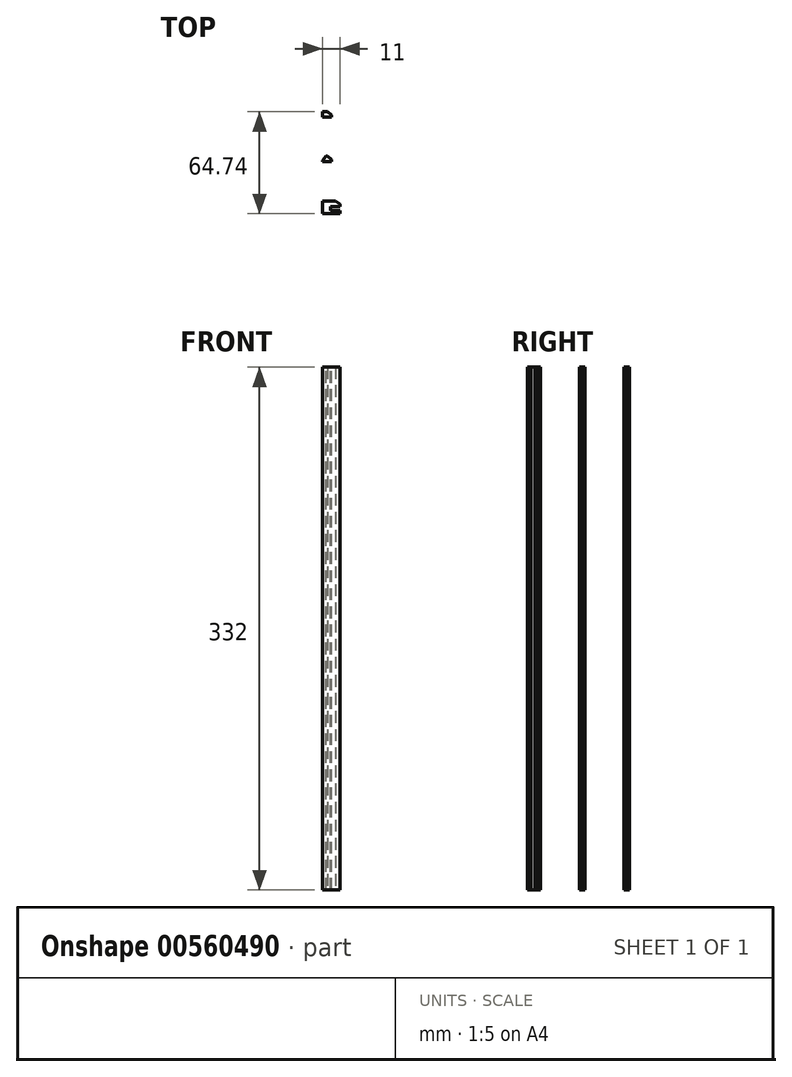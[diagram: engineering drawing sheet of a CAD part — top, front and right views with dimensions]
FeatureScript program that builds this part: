
annotation { "Feature Type Name" : "Feature", "Feature Type Description" : "" }
export const myFeature = defineFeature(function(context is Context, id is Id, definition is map)
    precondition{}
    {
        {
            var Q0;
            Q0=qCreatedBy(makeId("Top.planeOp"),FACE);
            var sketch = newSketch(context, id + "F0", { "sketchPlane" : qUnion([Q0])});
            skLineSegment(sketch, "E0.bottom", {"start": v(45.75, 4) * mm, "end": v(-45.75, 4) * mm});
            skLineSegment(sketch, "E0.top", {"start": v(45.75, -4) * mm, "end": v(-45.75, -4) * mm});
            skLineSegment(sketch, "E0.left", {"start": v(45.75, 4) * mm, "end": v(45.75, -4) * mm});
            skLineSegment(sketch, "E0.right", {"start": v(-45.75, 4) * mm, "end": v(-45.75, -4) * mm});
            skPoint(sketch, "E0.middle", {"position": v(0, 0) * mm});
            skLineSegment(sketch, "E1.bottom", {"start": v(45.75, -2) * mm, "end": v(39.75, -2) * mm});
            skLineSegment(sketch, "E1.top", {"start": v(45.75, 0.6) * mm, "end": v(39.75, 0.6) * mm});
            skLineSegment(sketch, "E1.left", {"start": v(45.75, -2) * mm, "end": v(45.75, 0.6) * mm});
            skLineSegment(sketch, "E1.right", {"start": v(39.75, -2) * mm, "end": v(39.75, 0.6) * mm});
            skPoint(sketch, "E1.middle", {"position": v(42.75, -0.7) * mm});
            skLineSegment(sketch, "E2.bottom", {"start": v(-45.75, -4) * mm, "end": v(-40.25, -4) * mm});
            skLineSegment(sketch, "E2.top", {"start": v(-45.75, -2) * mm, "end": v(-40.25, -2) * mm});
            skLineSegment(sketch, "E2.left", {"start": v(-45.75, -4) * mm, "end": v(-45.75, -2) * mm});
            skLineSegment(sketch, "E2.right", {"start": v(-40.25, -4) * mm, "end": v(-40.25, -2) * mm});
            skLineSegment(sketch, "E3.bottom", {"start": v(-45.75, 0.5) * mm, "end": v(-40.25, 0.5) * mm});
            skLineSegment(sketch, "E3.top", {"start": v(-45.75, 4) * mm, "end": v(-40.25, 4) * mm});
            skLineSegment(sketch, "E3.left", {"start": v(-45.75, 0.5) * mm, "end": v(-45.75, 4) * mm});
            skLineSegment(sketch, "E3.right", {"start": v(-40.25, 0.5) * mm, "end": v(-40.25, 4) * mm});
            skLineSegment(sketch, "E4.bottom", {"start": v(-34.82, -24.44) * mm, "end": v(-45.82, -24.44) * mm});
            skLineSegment(sketch, "E4.top", {"start": v(-34.82, -32.44) * mm, "end": v(-45.82, -32.44) * mm});
            skLineSegment(sketch, "E4.left", {"start": v(-34.82, -24.44) * mm, "end": v(-34.82, -32.44) * mm});
            skLineSegment(sketch, "E4.right", {"start": v(-45.82, -24.44) * mm, "end": v(-45.82, -32.44) * mm});
            skPoint(sketch, "E4.middle", {"position": v(-40.32, -28.44) * mm});
            skLineSegment(sketch, "E5.bottom", {"start": v(-34.82, -30.44) * mm, "end": v(-40.82, -30.44) * mm});
            skLineSegment(sketch, "E5.top", {"start": v(-34.82, -27.84) * mm, "end": v(-40.82, -27.84) * mm});
            skLineSegment(sketch, "E5.left", {"start": v(-34.82, -30.44) * mm, "end": v(-34.82, -27.84) * mm});
            skLineSegment(sketch, "E5.right", {"start": v(-40.82, -30.44) * mm, "end": v(-40.82, -27.84) * mm});
            skPoint(sketch, "E5.middle", {"position": v(-37.82, -29.14) * mm});
            skLineSegment(sketch, "E6.bottom", {"start": v(-45.82, -32.44) * mm, "end": v(-40.32, -32.44) * mm});
            skLineSegment(sketch, "E6.left", {"start": v(-45.82, -32.44) * mm, "end": v(-45.82, -30.44) * mm});
            skLineSegment(sketch, "E7.top", {"start": v(-45.82, -24.44) * mm, "end": v(-40.32, -24.44) * mm});
            skPoint(sketch, "E8.middle", {"position": v(-0.95, -28.36) * mm});
            skLineSegment(sketch, "E9.bottom", {"start": v(-29.23, 32.3) * mm, "end": v(-45.73, 32.3) * mm});
            skLineSegment(sketch, "E9.top", {"start": v(-29.23, 24.3) * mm, "end": v(-45.73, 24.3) * mm});
            skLineSegment(sketch, "E9.left", {"start": v(-29.23, 32.3) * mm, "end": v(-29.23, 24.3) * mm});
            skLineSegment(sketch, "E9.right", {"start": v(-45.73, 32.3) * mm, "end": v(-45.73, 24.3) * mm});
            skPoint(sketch, "E9.middle", {"position": v(-37.48, 28.3) * mm});
            skLineSegment(sketch, "E10.left", {"start": v(-29.23, 26.3) * mm, "end": v(-29.23, 28.9) * mm});
            skLineSegment(sketch, "E11.bottom", {"start": v(-45.73, 24.3) * mm, "end": v(-40.23, 24.3) * mm});
            skLineSegment(sketch, "E11.top", {"start": v(-45.73, 26.3) * mm, "end": v(-40.23, 26.3) * mm});
            skLineSegment(sketch, "E11.left", {"start": v(-45.73, 24.3) * mm, "end": v(-45.73, 26.3) * mm});
            skLineSegment(sketch, "E11.right", {"start": v(-40.23, 24.3) * mm, "end": v(-40.23, 26.3) * mm});
            skLineSegment(sketch, "E12.bottom", {"start": v(-45.73, 28.8) * mm, "end": v(-40.23, 28.8) * mm});
            skLineSegment(sketch, "E12.top", {"start": v(-45.73, 32.3) * mm, "end": v(-40.23, 32.3) * mm});
            skLineSegment(sketch, "E12.left", {"start": v(-45.73, 28.8) * mm, "end": v(-45.73, 32.3) * mm});
            skLineSegment(sketch, "E12.right", {"start": v(-40.23, 28.8) * mm, "end": v(-40.23, 32.3) * mm});
            skSolve(sketch);
        }
        {
            var Q0;
            {var subQ2=sQuery(id+"F0.wireOp",EDGE,"E0.bottom");Q0=makeQuery(id+"F0.imprint","IMPRINT",FACE,{"disambiguationData":[TD([[makeQuery(id+"F0.imprint","IMPRINT",EDGE,{"derivedFrom":subQ2}),1.0]])]});}
            extrude(context, id + "F1", {"entities" : qUnion([Q0]), "oppositeDirection" : true, "depth" : 332 * mm, "offsetDistance" : 25 * mm});
        }
        {
            var Q0;
            Q0=makeQuery(id+"F1.opExtrude","SWEPT_EDGE",EDGE,{"disambiguationData":[OSD([sQuery(id+"F0.wireOp",EDGE,"E0.bottom"),sQuery(id+"F0.wireOp",EDGE,"E3.top"),sQuery(id+"F0.wireOp",EDGE,"E3.right")])]});
            chamfer(context, id + "F2", {"entities" : qUnion([Q0]), "chamferType" : ChamferType.OFFSET_ANGLE, "width" : 2 * mm, "oppositeDirection" : false, "angle" : 50 * degree, "tangentPropagation" : true});
        }
        {
            var Q0;
            Q0=makeQuery(id+"F1.opExtrude","SWEPT_EDGE",EDGE,{"disambiguationData":[OSD([sQuery(id+"F0.wireOp",EDGE,"E0.bottom"),sQuery(id+"F0.wireOp",EDGE,"E0.left")])]});
            chamfer(context, id + "F3", {"entities" : qUnion([Q0]), "chamferType" : ChamferType.OFFSET_ANGLE, "width" : 2 * mm, "oppositeDirection" : false, "angle" : 55 * degree, "tangentPropagation" : true});
        }
        {
            var Q0;
            {var subQ3=sQuery(id+"F0.wireOp",EDGE,"E9.bottom");Q0=makeQuery(id+"F0.imprint","IMPRINT",FACE,{"disambiguationData":[TD([[makeQuery(id+"F0.imprint","IMPRINT",EDGE,{"derivedFrom":subQ3}),1.0]])]});}
            extrude(context, id + "F4", {"entities" : qUnion([Q0]), "oppositeDirection" : true, "depth" : 332 * mm, "offsetDistance" : 25 * mm});
        }
        {
            var Q0;
            {var subQ2=sQuery(id+"F0.wireOp",EDGE,"E4.bottom");Q0=makeQuery(id+"F0.imprint","IMPRINT",FACE,{"disambiguationData":[TD([[makeQuery(id+"F0.imprint","IMPRINT",EDGE,{"derivedFrom":subQ2}),1.0]])]});}
            extrude(context, id + "F5", {"entities" : qUnion([Q0]), "oppositeDirection" : true, "depth" : 332 * mm, "offsetDistance" : 25 * mm});
        }
        {
            var Q0;
            Q0=makeQuery(id+"F4.opExtrude","SWEPT_EDGE",EDGE,{"disambiguationData":[OSD([sQuery(id+"F0.wireOp",EDGE,"E9.bottom"),sQuery(id+"F0.wireOp",EDGE,"E12.top"),sQuery(id+"F0.wireOp",EDGE,"E12.right")])]});
            chamfer(context, id + "F6", {"entities" : qUnion([Q0]), "chamferType" : ChamferType.OFFSET_ANGLE, "width" : 2 * mm, "oppositeDirection" : false, "angle" : 50 * degree, "tangentPropagation" : true});
        }
        {
            var Q0;
            Q0=makeQuery(id+"F5.opExtrude","SWEPT_EDGE",EDGE,{"disambiguationData":[OSD([sQuery(id+"F0.wireOp",EDGE,"E4.bottom"),sQuery(id+"F0.wireOp",EDGE,"E4.left")])]});
            chamfer(context, id + "F7", {"entities" : qUnion([Q0]), "chamferType" : ChamferType.OFFSET_ANGLE, "width" : 2 * mm, "oppositeDirection" : false, "angle" : 55 * degree, "tangentPropagation" : true});
        }
    });
